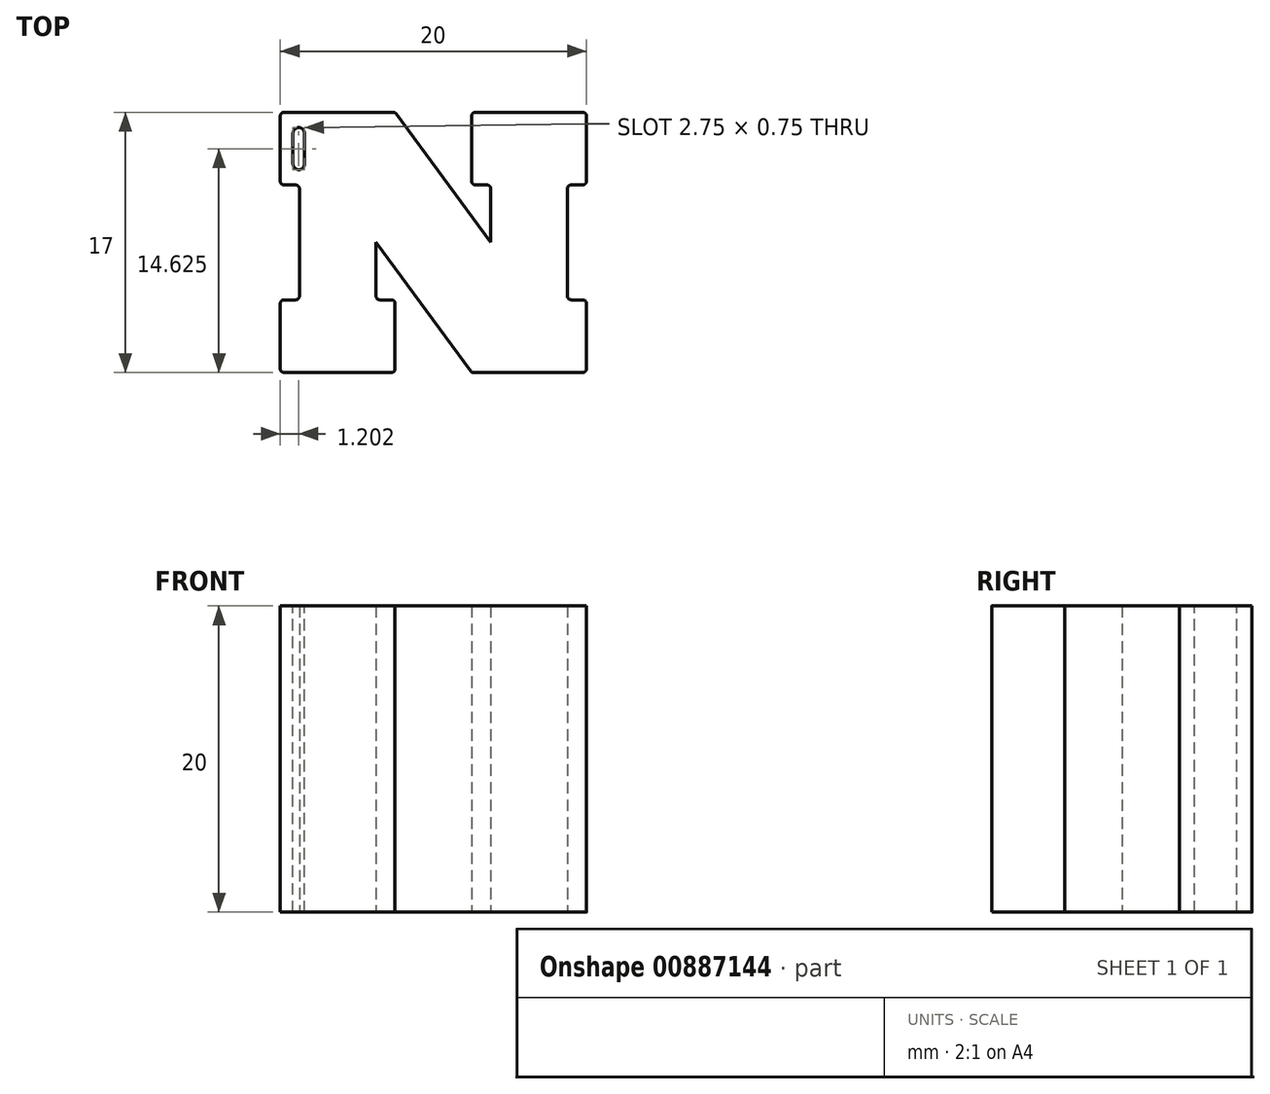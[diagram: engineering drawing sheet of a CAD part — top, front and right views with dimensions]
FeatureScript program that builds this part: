
annotation { "Feature Type Name" : "Feature", "Feature Type Description" : "" }
export const myFeature = defineFeature(function(context is Context, id is Id, definition is map)
    precondition{}
    {
        {
            var Q0;
            Q0=qCreatedBy(makeId("Top.planeOp"),FACE);
            var sketch = newSketch(context, id + "F0", { "sketchPlane" : qUnion([Q0])});
            skLineSegment(sketch, "E0.top", {"start": v(-10, 3.75) * mm, "end": v(-8.75, 3.75) * mm});
            skLineSegment(sketch, "E0.left", {"start": v(-10, 8.5) * mm, "end": v(-10, 3.75) * mm});
            skLineSegment(sketch, "E0.right", {"start": v(10, 8.5) * mm, "end": v(10, 3.75) * mm});
            skLineSegment(sketch, "E1.bottom", {"start": v(-10, -3.75) * mm, "end": v(-8.75, -3.75) * mm});
            skLineSegment(sketch, "E1.left", {"start": v(-10, -3.75) * mm, "end": v(-10, -8.5) * mm});
            skLineSegment(sketch, "E1.right", {"start": v(10, -3.75) * mm, "end": v(10, -8.5) * mm});
            skLineSegment(sketch, "E2.left", {"start": v(-8.75, 3.75) * mm, "end": v(-8.75, -3.75) * mm});
            skLineSegment(sketch, "E2.right", {"start": v(-3.75, 0) * mm, "end": v(-3.75, -3.75) * mm});
            skLineSegment(sketch, "E3.left", {"start": v(3.75, 0) * mm, "end": v(3.75, 3.75) * mm});
            skLineSegment(sketch, "E3.right", {"start": v(8.75, -3.75) * mm, "end": v(8.75, 3.75) * mm});
            skLineSegment(sketch, "E4", {"start": v(2.5, 3.75) * mm, "end": v(2.5, 8.5) * mm});
            skLineSegment(sketch, "E5.trimOffspring", {"start": v(2.5, 3.75) * mm, "end": v(3.75, 3.75) * mm});
            skLineSegment(sketch, "E6.trimOffspring", {"start": v(8.75, 3.75) * mm, "end": v(10, 3.75) * mm});
            skLineSegment(sketch, "E7", {"start": v(-2.5, -3.75) * mm, "end": v(-2.5, -8.5) * mm});
            skLineSegment(sketch, "E8.trimOffspring", {"start": v(2.5, -8.5) * mm, "end": v(10, -8.5) * mm});
            skLineSegment(sketch, "E9.trimOffspring", {"start": v(-3.75, -3.75) * mm, "end": v(-2.5, -3.75) * mm});
            skLineSegment(sketch, "E10.trimOffspring", {"start": v(8.75, -3.75) * mm, "end": v(10, -3.75) * mm});
            skLineSegment(sketch, "E11", {"start": v(-10, 8.5) * mm, "end": v(-2.5, 8.5) * mm});
            skLineSegment(sketch, "E12", {"start": v(2.5, 8.5) * mm, "end": v(10, 8.5) * mm});
            skLineSegment(sketch, "E13", {"start": v(-10, -8.5) * mm, "end": v(-2.5, -8.5) * mm});
            skLineSegment(sketch, "E14", {"start": v(-3.75, 0) * mm, "end": v(2.5, -8.5) * mm});
            skLineSegment(sketch, "E15", {"start": v(3.75, 0) * mm, "end": v(-2.5, 8.5) * mm});
            skSolve(sketch);
        }
        {
            var Q0;
            Q0=makeQuery(id+"F0.imprint","IMPRINT",FACE,{"disambiguationData":[TD([[makeQuery(id+"F0.imprint","IMPRINT",EDGE,{"derivedFrom":sQuery(id+"F0.wireOp",EDGE,"E0.top")}),1.0]])]});
            extrude(context, id + "F1", {"entities" : qUnion([Q0]), "depth" : 20 * mm, "offsetDistance" : 25 * mm});
        }
        {
            var Q0;
            Q0=makeQuery(id+"F1.opExtrude","CAP_FACE",FACE,{"disambiguationData":[OSD([sQuery(id+"F0.wireOp",EDGE,"E0.top"),sQuery(id+"F0.wireOp",EDGE,"E0.left"),sQuery(id+"F0.wireOp",EDGE,"E0.right"),sQuery(id+"F0.wireOp",EDGE,"E1.bottom"),sQuery(id+"F0.wireOp",EDGE,"E1.left"),sQuery(id+"F0.wireOp",EDGE,"E1.right"),sQuery(id+"F0.wireOp",EDGE,"E2.left"),sQuery(id+"F0.wireOp",EDGE,"E2.right"),sQuery(id+"F0.wireOp",EDGE,"E3.left"),sQuery(id+"F0.wireOp",EDGE,"E3.right"),sQuery(id+"F0.wireOp",EDGE,"E4"),sQuery(id+"F0.wireOp",EDGE,"E5.trimOffspring"),sQuery(id+"F0.wireOp",EDGE,"E6.trimOffspring"),sQuery(id+"F0.wireOp",EDGE,"E7"),sQuery(id+"F0.wireOp",EDGE,"E8.trimOffspring"),sQuery(id+"F0.wireOp",EDGE,"E9.trimOffspring"),sQuery(id+"F0.wireOp",EDGE,"E10.trimOffspring"),sQuery(id+"F0.wireOp",EDGE,"E11"),sQuery(id+"F0.wireOp",EDGE,"E12"),sQuery(id+"F0.wireOp",EDGE,"E13"),sQuery(id+"F0.wireOp",EDGE,"E14"),sQuery(id+"F0.wireOp",EDGE,"E15")])],"isStart":false});
            var sketch = newSketch(context, id + "F2", { "sketchPlane" : qUnion([Q0])});
            skLineSegment(sketch, "E16.left", {"start": v(-9.17, 7.12) * mm, "end": v(-9.17, 5.12) * mm});
            skLineSegment(sketch, "E16.right", {"start": v(-8.42, 7.12) * mm, "end": v(-8.42, 5.12) * mm});
            skLineSegment(sketch, "E17", {"start": v(-10, 6.12) * mm, "end": v(10, 6.12) * mm, "construction": true});
            skArc(sketch, "E18", {"start": v(-8.42, 7.12) * mm, "mid": v(-8.8, 7.5) * mm, "end": v(-9.17, 7.12) * mm});
            skArc(sketch, "E19", {"start": v(-9.17, 5.12) * mm, "mid": v(-8.8, 4.75) * mm, "end": v(-8.42, 5.12) * mm});
            skSolve(sketch);
        }
        {
            var Q0;
            Q0=makeQuery(id+"F2.imprint","IMPRINT",FACE,{"disambiguationData":[TD([[makeQuery(id+"F2.imprint","IMPRINT",EDGE,{"derivedFrom":sQuery(id+"F2.wireOp",EDGE,"E16.left")}),1.0]])]});
            extrude(context, id + "F3", {"entities" : qUnion([Q0]), "operationType" : NewBodyOperationType.REMOVE, "oppositeDirection" : true, "depth" : 25 * mm, "offsetDistance" : 25 * mm});
        }
        {
            var Q0;
            Q0=makeQuery(id+"F1.opExtrude","SWEPT_EDGE",EDGE,{"disambiguationData":[OSD([sQuery(id+"F0.wireOp",EDGE,"E0.left"),sQuery(id+"F0.wireOp",EDGE,"E11")])]});
            var Q1;
            Q1=makeQuery(id+"F1.opExtrude","SWEPT_EDGE",EDGE,{"disambiguationData":[OSD([sQuery(id+"F0.wireOp",EDGE,"E4"),sQuery(id+"F0.wireOp",EDGE,"E12")])]});
            var Q2;
            Q2=makeQuery(id+"F1.opExtrude","SWEPT_EDGE",EDGE,{"disambiguationData":[OSD([sQuery(id+"F0.wireOp",EDGE,"E11"),sQuery(id+"F0.wireOp",EDGE,"E15")])]});
            var Q3;
            Q3=makeQuery(id+"F1.opExtrude","SWEPT_EDGE",EDGE,{"disambiguationData":[OSD([sQuery(id+"F0.wireOp",EDGE,"E4"),sQuery(id+"F0.wireOp",EDGE,"E5.trimOffspring")])]});
            var Q4;
            Q4=makeQuery(id+"F1.opExtrude","SWEPT_EDGE",EDGE,{"disambiguationData":[OSD([sQuery(id+"F0.wireOp",EDGE,"E0.right"),sQuery(id+"F0.wireOp",EDGE,"E6.trimOffspring")])]});
            var Q5;
            Q5=makeQuery(id+"F1.opExtrude","SWEPT_EDGE",EDGE,{"disambiguationData":[OSD([sQuery(id+"F0.wireOp",EDGE,"E0.right"),sQuery(id+"F0.wireOp",EDGE,"E12")])]});
            var Q6;
            Q6=makeQuery(id+"F1.opExtrude","SWEPT_EDGE",EDGE,{"disambiguationData":[OSD([sQuery(id+"F0.wireOp",EDGE,"E1.right"),sQuery(id+"F0.wireOp",EDGE,"E10.trimOffspring")])]});
            var Q7;
            Q7=makeQuery(id+"F1.opExtrude","SWEPT_EDGE",EDGE,{"disambiguationData":[OSD([sQuery(id+"F0.wireOp",EDGE,"E1.right"),sQuery(id+"F0.wireOp",EDGE,"E8.trimOffspring")])]});
            var Q8;
            Q8=makeQuery(id+"F1.opExtrude","SWEPT_EDGE",EDGE,{"disambiguationData":[OSD([sQuery(id+"F0.wireOp",EDGE,"E8.trimOffspring"),sQuery(id+"F0.wireOp",EDGE,"E14")])]});
            var Q9;
            Q9=makeQuery(id+"F1.opExtrude","SWEPT_EDGE",EDGE,{"disambiguationData":[OSD([sQuery(id+"F0.wireOp",EDGE,"E7"),sQuery(id+"F0.wireOp",EDGE,"E9.trimOffspring")])]});
            var Q10;
            Q10=makeQuery(id+"F1.opExtrude","SWEPT_EDGE",EDGE,{"disambiguationData":[OSD([sQuery(id+"F0.wireOp",EDGE,"E7"),sQuery(id+"F0.wireOp",EDGE,"E13")])]});
            var Q11;
            Q11=makeQuery(id+"F1.opExtrude","SWEPT_EDGE",EDGE,{"disambiguationData":[OSD([sQuery(id+"F0.wireOp",EDGE,"E1.left"),sQuery(id+"F0.wireOp",EDGE,"E13")])]});
            var Q12;
            Q12=makeQuery(id+"F1.opExtrude","SWEPT_EDGE",EDGE,{"disambiguationData":[OSD([sQuery(id+"F0.wireOp",EDGE,"E1.bottom"),sQuery(id+"F0.wireOp",EDGE,"E1.left")])]});
            var Q13;
            Q13=makeQuery(id+"F1.opExtrude","SWEPT_EDGE",EDGE,{"disambiguationData":[OSD([sQuery(id+"F0.wireOp",EDGE,"E1.bottom"),sQuery(id+"F0.wireOp",EDGE,"E2.left")])]});
            var Q14;
            Q14=makeQuery(id+"F1.opExtrude","SWEPT_EDGE",EDGE,{"disambiguationData":[OSD([sQuery(id+"F0.wireOp",EDGE,"E2.right"),sQuery(id+"F0.wireOp",EDGE,"E9.trimOffspring")])]});
            var Q15;
            Q15=makeQuery(id+"F1.opExtrude","SWEPT_EDGE",EDGE,{"disambiguationData":[OSD([sQuery(id+"F0.wireOp",EDGE,"E0.top"),sQuery(id+"F0.wireOp",EDGE,"E2.left")])]});
            var Q16;
            Q16=makeQuery(id+"F1.opExtrude","SWEPT_EDGE",EDGE,{"disambiguationData":[OSD([sQuery(id+"F0.wireOp",EDGE,"E0.top"),sQuery(id+"F0.wireOp",EDGE,"E0.left")])]});
            var Q17;
            Q17=makeQuery(id+"F1.opExtrude","SWEPT_EDGE",EDGE,{"disambiguationData":[OSD([sQuery(id+"F0.wireOp",EDGE,"E3.left"),sQuery(id+"F0.wireOp",EDGE,"E5.trimOffspring")])]});
            var Q18;
            Q18=makeQuery(id+"F1.opExtrude","SWEPT_EDGE",EDGE,{"disambiguationData":[OSD([sQuery(id+"F0.wireOp",EDGE,"E3.right"),sQuery(id+"F0.wireOp",EDGE,"E6.trimOffspring")])]});
            var Q19;
            Q19=makeQuery(id+"F1.opExtrude","SWEPT_EDGE",EDGE,{"disambiguationData":[OSD([sQuery(id+"F0.wireOp",EDGE,"E3.right"),sQuery(id+"F0.wireOp",EDGE,"E10.trimOffspring")])]});
            fillet(context, id + "F4", {"entities" : qUnion([Q0, Q1, Q2, Q3, Q4, Q5, Q6, Q7, Q8, Q9, Q10, Q11, Q12, Q13, Q14, Q15, Q16, Q17, Q18, Q19]), "radius" : .25 * mm, "tangentPropagation" : true, "allowEdgeOverflow" : false});
        }
    });
